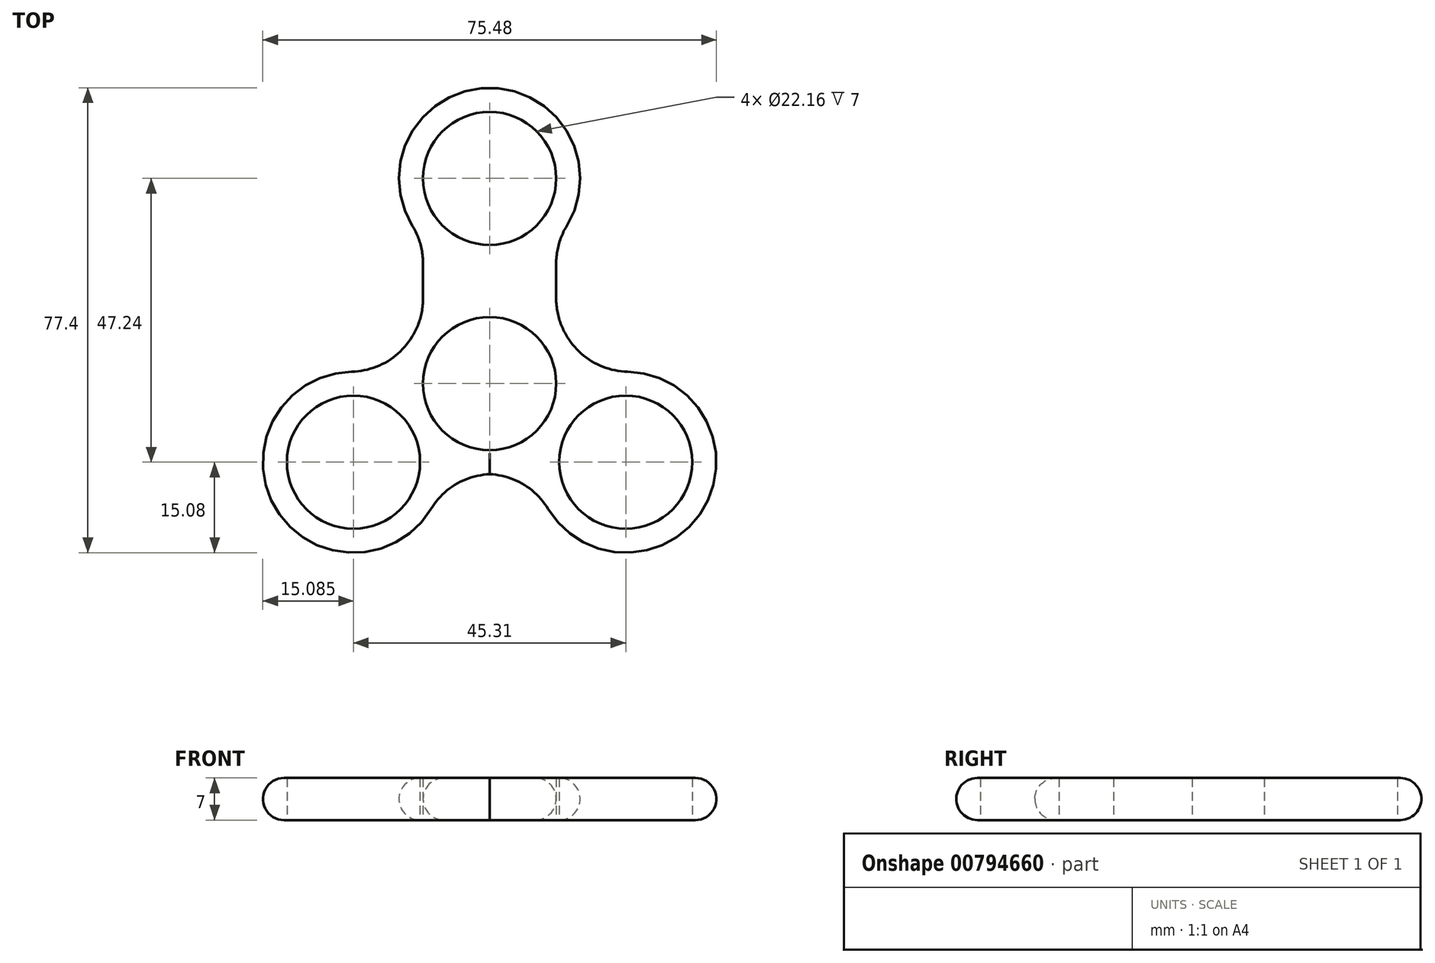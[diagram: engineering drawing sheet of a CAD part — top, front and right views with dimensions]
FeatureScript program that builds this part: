
annotation { "Feature Type Name" : "Feature", "Feature Type Description" : "" }
export const myFeature = defineFeature(function(context is Context, id is Id, definition is map)
    precondition{}
    {
        {
            var Q0;
            Q0=qCreatedBy(makeId("Top.planeOp"),FACE);
            var sketch = newSketch(context, id + "F0", { "sketchPlane" : qUnion([Q0])});
            skCircle(sketch, "E0", {"center": v(0, 0) * mm, "radius": 11.08 * mm});
            skCircle(sketch, "E1", {"center": v(0, 34.16) * mm, "radius": 11.08 * mm});
            skCircle(sketch, "E2.1.0", {"center": v(-22.66, -13.08) * mm, "radius": 11.08 * mm});
            skCircle(sketch, "E2.2.0", {"center": v(22.66, -13.08) * mm, "radius": 11.08 * mm});
            skCircle(sketch, "E3", {"center": v(0, 34.16) * mm, "radius": 15.08 * mm});
            skCircle(sketch, "E4", {"center": v(-22.66, -13.08) * mm, "radius": 15.08 * mm});
            skCircle(sketch, "E5", {"center": v(0, 0) * mm, "radius": 15.08 * mm});
            skCircle(sketch, "E6", {"center": v(22.66, -13.08) * mm, "radius": 15.08 * mm});
            skLineSegment(sketch, "E7", {"start": v(-11.08, 34.16) * mm, "end": v(-11.08, 10.23) * mm});
            skLineSegment(sketch, "E8", {"start": v(11.08, 34.16) * mm, "end": v(11.08, 10.23) * mm});
            skSolve(sketch);
        }
        {
            var Q0;
            {var subQ0=sQuery(id+"F0.wireOp",EDGE,"E7");var subQ1=sQuery(id+"F0.wireOp",EDGE,"E1");var subQ2=makeQuery(id+"F0.imprint","INTERSECT",VERTEX,{"derivedFrom":[subQ1,subQ0]});Q0=makeQuery(id+"F0.imprint","IMPRINT",FACE,{"disambiguationData":[TD([[makeQuery(id+"F0.imprint","IMPRINT",EDGE,{"disambiguationData":[TD([[subQ2,1.0]])],"derivedFrom":subQ1}),-1.0]])]});}
            var Q1;
            {var subQ0=sQuery(id+"F0.wireOp",EDGE,"E7");var subQ1=sQuery(id+"F0.wireOp",EDGE,"E1");var subQ2=makeQuery(id+"F0.imprint","INTERSECT",VERTEX,{"derivedFrom":[subQ1,subQ0]});Q1=makeQuery(id+"F0.imprint","IMPRINT",FACE,{"disambiguationData":[TD([[makeQuery(id+"F0.imprint","IMPRINT",EDGE,{"disambiguationData":[TD([[subQ2,-1.0]])],"derivedFrom":subQ1}),-1.0]])]});}
            var Q2;
            {var subQ0=sQuery(id+"F0.wireOp",EDGE,"E7");var subQ1=sQuery(id+"F0.wireOp",EDGE,"E3");var subQ2=makeQuery(id+"F0.imprint","INTERSECT",VERTEX,{"derivedFrom":[subQ1,subQ0]});Q2=makeQuery(id+"F0.imprint","IMPRINT",FACE,{"disambiguationData":[TD([[makeQuery(id+"F0.imprint","IMPRINT",EDGE,{"disambiguationData":[TD([[subQ2,-1.0]])],"derivedFrom":subQ1}),-1.0]])]});}
            var Q3;
            Q3=makeQuery(id+"F0.imprint","IMPRINT",FACE,{"disambiguationData":[TD([[makeQuery(id+"F0.imprint","IMPRINT",EDGE,{"derivedFrom":sQuery(id+"F0.wireOp",EDGE,"E0")}),-1.0]])]});
            var Q4;
            Q4=makeQuery(id+"F0.imprint","IMPRINT",FACE,{"disambiguationData":[TD([[makeQuery(id+"F0.imprint","IMPRINT",EDGE,{"derivedFrom":sQuery(id+"F0.wireOp",EDGE,"E2.1.0")}),-1.0]])]});
            var Q5;
            Q5=makeQuery(id+"F0.imprint","IMPRINT",FACE,{"disambiguationData":[TD([[makeQuery(id+"F0.imprint","IMPRINT",EDGE,{"derivedFrom":sQuery(id+"F0.wireOp",EDGE,"E2.2.0")}),-1.0]])]});
            var Q6;
            {var subQ0=sQuery(id+"F0.wireOp",EDGE,"E5");var subQ1=sQuery(id+"F0.wireOp",EDGE,"E4");var subQ2=makeQuery(id+"F0.imprint","INTERSECT",VERTEX,{"disambiguationData":[OD(0.0)],"derivedFrom":[subQ1,subQ0]});Q6=makeQuery(id+"F0.imprint","IMPRINT",FACE,{"disambiguationData":[TD([[makeQuery(id+"F0.imprint","IMPRINT",EDGE,{"disambiguationData":[TD([[subQ2,-1.0]])],"derivedFrom":subQ1}),1.0]])]});}
            var Q7;
            {var subQ0=sQuery(id+"F0.wireOp",EDGE,"E5");var subQ1=makeQuery(id+"F0.imprint","INTERSECT",VERTEX,{"derivedFrom":[sQuery(id+"F0.wireOp",EDGE,"E2.2.0"),subQ0]});Q7=makeQuery(id+"F0.imprint","IMPRINT",FACE,{"disambiguationData":[TD([[makeQuery(id+"F0.imprint","IMPRINT",EDGE,{"disambiguationData":[TD([[subQ1,1.0]])],"derivedFrom":subQ0}),1.0]])]});}
            var Q8;
            {var subQ2=sQuery(id+"F0.wireOp",EDGE,"E4");var subQ4=sQuery(id+"F0.wireOp",EDGE,"E0");var subQ5=makeQuery(id+"F0.imprint","INTERSECT",VERTEX,{"derivedFrom":[subQ4,subQ2]});Q8=makeQuery(id+"F0.imprint","IMPRINT",FACE,{"disambiguationData":[TD([[makeQuery(id+"F0.imprint","IMPRINT",EDGE,{"disambiguationData":[TD([[subQ5,1.0]])],"derivedFrom":subQ4}),-1.0]])]});}
            extrude(context, id + "F1", {"entities" : qUnion([Q0, Q1, Q2, Q3, Q4, Q5, Q6, Q7, Q8]), "depth" : 7 * mm, "offsetDistance" : 25 * mm});
        }
        {
            var Q0;
            {var subQ0=sQuery(id+"F0.wireOp",EDGE,"E6");var subQ1=sQuery(id+"F0.wireOp",EDGE,"E5");Q0=makeQuery(id+"F1.opExtrude","SWEPT_EDGE",EDGE,{"disambiguationData":[OSD([subQ1,subQ0]),TDD([makeQuery(id+"F0.imprint","INTERSECT",VERTEX,{"disambiguationData":[OD(1.0)],"derivedFrom":[subQ1,subQ0]})])]});}
            var Q1;
            Q1=makeQuery(id+"F1.opExtrude","SWEPT_EDGE",EDGE,{"disambiguationData":[OSD([sQuery(id+"F0.wireOp",EDGE,"E5"),sQuery(id+"F0.wireOp",EDGE,"E8")])]});
            var Q2;
            Q2=makeQuery(id+"F1.opExtrude","SWEPT_EDGE",EDGE,{"disambiguationData":[OSD([sQuery(id+"F0.wireOp",EDGE,"E3"),sQuery(id+"F0.wireOp",EDGE,"E8")])]});
            var Q3;
            Q3=makeQuery(id+"F1.opExtrude","SWEPT_EDGE",EDGE,{"disambiguationData":[OSD([sQuery(id+"F0.wireOp",EDGE,"E3"),sQuery(id+"F0.wireOp",EDGE,"E7")])]});
            var Q4;
            Q4=makeQuery(id+"F1.opExtrude","SWEPT_EDGE",EDGE,{"disambiguationData":[OSD([sQuery(id+"F0.wireOp",EDGE,"E5"),sQuery(id+"F0.wireOp",EDGE,"E7")])]});
            var Q5;
            {var subQ0=sQuery(id+"F0.wireOp",EDGE,"E5");var subQ1=sQuery(id+"F0.wireOp",EDGE,"E4");Q5=makeQuery(id+"F1.opExtrude","SWEPT_EDGE",EDGE,{"disambiguationData":[OSD([subQ1,subQ0]),TDD([makeQuery(id+"F0.imprint","INTERSECT",VERTEX,{"disambiguationData":[OD(1.0)],"derivedFrom":[subQ1,subQ0]})])]});}
            var Q6;
            {var subQ0=sQuery(id+"F0.wireOp",EDGE,"E5");var subQ1=sQuery(id+"F0.wireOp",EDGE,"E4");Q6=makeQuery(id+"F1.opExtrude","SWEPT_EDGE",EDGE,{"disambiguationData":[OSD([subQ1,subQ0]),TDD([makeQuery(id+"F0.imprint","INTERSECT",VERTEX,{"disambiguationData":[OD(0.0)],"derivedFrom":[subQ1,subQ0]})])]});}
            var Q7;
            {var subQ0=sQuery(id+"F0.wireOp",EDGE,"E6");var subQ1=sQuery(id+"F0.wireOp",EDGE,"E5");Q7=makeQuery(id+"F1.opExtrude","SWEPT_EDGE",EDGE,{"disambiguationData":[OSD([subQ1,subQ0]),TDD([makeQuery(id+"F0.imprint","INTERSECT",VERTEX,{"disambiguationData":[OD(0.0)],"derivedFrom":[subQ1,subQ0]})])]});}
            fillet(context, id + "F2", {"entities" : qUnion([Q0, Q1, Q2, Q3, Q4, Q5, Q6, Q7]), "radius" : 12 * mm, "tangentPropagation" : true, "allowEdgeOverflow" : false});
        }
        {
            var Q0;
            Q0=makeQuery(id+"F1.opExtrude","CAP_EDGE",EDGE,{"disambiguationData":[OSD([sQuery(id+"F0.wireOp",EDGE,"E7")])],"isStart":true});
            var Q1;
            {var subQ0=sQuery(id+"F0.wireOp",EDGE,"E7");var subQ1=sQuery(id+"F0.wireOp",EDGE,"E3");Q1=makeQuery(id+"F2.opFillet","BLEND_EDGE",EDGE,{"blendedFrom":[makeQuery(id+"F1.opExtrude","SWEPT_EDGE",EDGE,{"disambiguationData":[OSD([subQ1,subQ0])]}),makeQuery(id+"F1.opExtrude","CAP_FACE",FACE,{"disambiguationData":[OSD([sQuery(id+"F0.wireOp",EDGE,"E0"),sQuery(id+"F0.wireOp",EDGE,"E1"),sQuery(id+"F0.wireOp",EDGE,"E2.1.0"),sQuery(id+"F0.wireOp",EDGE,"E2.2.0"),subQ1,sQuery(id+"F0.wireOp",EDGE,"E4"),sQuery(id+"F0.wireOp",EDGE,"E5"),sQuery(id+"F0.wireOp",EDGE,"E6"),subQ0,sQuery(id+"F0.wireOp",EDGE,"E8")])],"isStart":false})],"blendedInto":[makeQuery(id+"F1.opExtrude","CAP_FACE",FACE,{"disambiguationData":[OSD([sQuery(id+"F0.wireOp",EDGE,"E0"),sQuery(id+"F0.wireOp",EDGE,"E1"),sQuery(id+"F0.wireOp",EDGE,"E2.1.0"),sQuery(id+"F0.wireOp",EDGE,"E2.2.0"),subQ1,sQuery(id+"F0.wireOp",EDGE,"E4"),sQuery(id+"F0.wireOp",EDGE,"E5"),sQuery(id+"F0.wireOp",EDGE,"E6"),subQ0,sQuery(id+"F0.wireOp",EDGE,"E8")])],"isStart":false})]});}
            fillet(context, id + "F3", {"entities" : qUnion([Q0, Q1]), "radius" : 3.5 * mm, "tangentPropagation" : true, "allowEdgeOverflow" : false});
        }
    });
